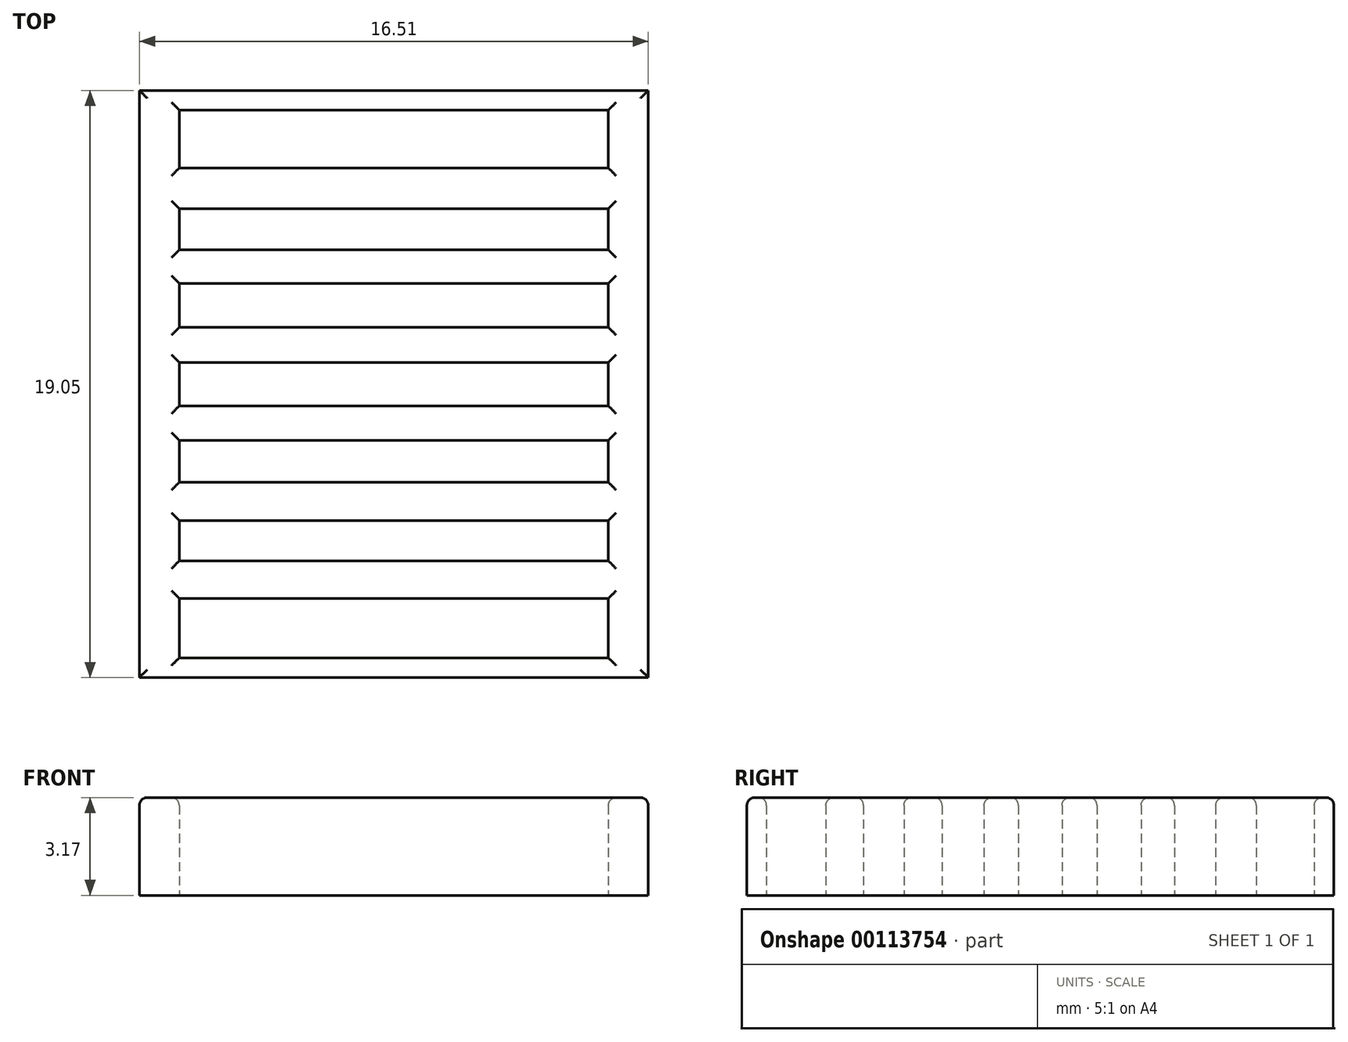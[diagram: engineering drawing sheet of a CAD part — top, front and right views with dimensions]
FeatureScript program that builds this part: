
annotation { "Feature Type Name" : "Feature", "Feature Type Description" : "" }
export const myFeature = defineFeature(function(context is Context, id is Id, definition is map)
    precondition{}
    {
        {
            var Q0;
            Q0=qCreatedBy(makeId("Top.planeOp"),FACE);
            var sketch = newSketch(context, id + "F0", { "sketchPlane" : qUnion([Q0])});
            skLineSegment(sketch, "E0.bottom", {"start": v(7.13, 8.73) * mm, "end": v(-6.8, 8.73) * mm});
            skLineSegment(sketch, "E0.top", {"start": v(7.13, -9.05) * mm, "end": v(-6.8, -9.05) * mm});
            skLineSegment(sketch, "E0.left", {"start": v(7.13, 8.73) * mm, "end": v(7.13, 6.84) * mm});
            skLineSegment(sketch, "E0.right", {"start": v(-6.8, 8.73) * mm, "end": v(-6.8, 6.84) * mm});
            skPoint(sketch, "E0.middle", {"position": v(0.16, -0.16) * mm});
            skPoint(sketch, "E1.orphan", {"position": v(-6.8, -0.16) * mm});
            skPoint(sketch, "E2.start.orphan", {"position": v(7.13, -0.16) * mm});
            skLineSegment(sketch, "E3.bottom", {"start": v(8.42, 9.36) * mm, "end": v(-8.1, 9.36) * mm});
            skLineSegment(sketch, "E3.top", {"start": v(8.42, -9.69) * mm, "end": v(-8.1, -9.69) * mm});
            skLineSegment(sketch, "E3.left", {"start": v(8.42, 9.36) * mm, "end": v(8.42, -9.69) * mm});
            skLineSegment(sketch, "E3.right", {"start": v(-8.1, 9.36) * mm, "end": v(-8.1, -9.69) * mm});
            skLineSegment(sketch, "E4.bottom", {"start": v(7.13, 5.53) * mm, "end": v(-6.8, 5.53) * mm});
            skLineSegment(sketch, "E4.top", {"start": v(7.13, 6.84) * mm, "end": v(-6.8, 6.84) * mm});
            skPoint(sketch, "E4.middle", {"position": v(0.16, 6.19) * mm});
            skLineSegment(sketch, "E5.bottom", {"start": v(7.13, 3.1) * mm, "end": v(-6.8, 3.1) * mm});
            skLineSegment(sketch, "E5.top", {"start": v(7.13, 4.19) * mm, "end": v(-6.8, 4.19) * mm});
            skPoint(sketch, "E5.middle", {"position": v(0.16, 3.65) * mm});
            skLineSegment(sketch, "E6.bottom", {"start": v(7.13, 0.54) * mm, "end": v(-6.8, 0.54) * mm});
            skLineSegment(sketch, "E6.top", {"start": v(7.13, 1.67) * mm, "end": v(-6.8, 1.67) * mm});
            skPoint(sketch, "E6.middle", {"position": v(0.16, 1.1) * mm});
            skLineSegment(sketch, "E7.bottom", {"start": v(7.13, -2) * mm, "end": v(-6.8, -2) * mm});
            skLineSegment(sketch, "E7.top", {"start": v(7.13, -0.88) * mm, "end": v(-6.8, -0.88) * mm});
            skPoint(sketch, "E7.middle", {"position": v(0.16, -1.43) * mm});
            skLineSegment(sketch, "E8.bottom", {"start": v(7.13, -4.6) * mm, "end": v(-6.8, -4.6) * mm});
            skLineSegment(sketch, "E8.top", {"start": v(7.13, -3.36) * mm, "end": v(-6.8, -3.36) * mm});
            skPoint(sketch, "E8.middle", {"position": v(0.16, -3.97) * mm});
            skLineSegment(sketch, "E9.bottom", {"start": v(7.13, -7.12) * mm, "end": v(-6.8, -7.12) * mm});
            skLineSegment(sketch, "E9.top", {"start": v(7.13, -5.9) * mm, "end": v(-6.8, -5.9) * mm});
            skPoint(sketch, "E9.middle", {"position": v(0.16, -6.51) * mm});
            skLineSegment(sketch, "E10.trimOffspring", {"start": v(-6.8, 5.53) * mm, "end": v(-6.8, 4.19) * mm});
            skLineSegment(sketch, "E11.trimOffspring", {"start": v(-6.8, 3.1) * mm, "end": v(-6.8, 1.67) * mm});
            skLineSegment(sketch, "E12.trimOffspring", {"start": v(-6.8, 0.54) * mm, "end": v(-6.8, -0.16) * mm});
            skLineSegment(sketch, "E13.trimOffspring", {"start": v(-6.8, -2) * mm, "end": v(-6.8, -3.36) * mm});
            skLineSegment(sketch, "E14.trimOffspring", {"start": v(-6.8, -4.6) * mm, "end": v(-6.8, -5.9) * mm});
            skLineSegment(sketch, "E15.trimOffspring", {"start": v(-6.8, -7.12) * mm, "end": v(-6.8, -9.05) * mm});
            skLineSegment(sketch, "E16.trimOffspring", {"start": v(7.13, -7.12) * mm, "end": v(7.13, -9.05) * mm});
            skLineSegment(sketch, "E17.trimOffspring", {"start": v(7.13, -4.6) * mm, "end": v(7.13, -5.9) * mm});
            skLineSegment(sketch, "E18.trimOffspring", {"start": v(7.13, -2) * mm, "end": v(7.13, -3.36) * mm});
            skLineSegment(sketch, "E19.trimOffspring", {"start": v(7.13, 0.54) * mm, "end": v(7.13, -0.88) * mm});
            skLineSegment(sketch, "E20.trimOffspring", {"start": v(7.13, 3.1) * mm, "end": v(7.13, 1.67) * mm});
            skLineSegment(sketch, "E21.trimOffspring", {"start": v(7.13, 5.53) * mm, "end": v(7.13, 4.19) * mm});
            skLineSegment(sketch, "E22", {"start": v(-6.8, -0.88) * mm, "end": v(-6.8, -0.16) * mm});
            skSolve(sketch);
        }
        {
            var Q0;
            Q0=makeQuery(id+"F0.imprint","IMPRINT",FACE,{"disambiguationData":[TD([[makeQuery(id+"F0.imprint","IMPRINT",EDGE,{"derivedFrom":sQuery(id+"F0.wireOp",EDGE,"E0.bottom")}),-1.0]])]});
            extrude(context, id + "F1", {"entities" : qUnion([Q0]), "depth" : 3.17 * mm});
        }
        {
            var Q0;
            Q0=makeQuery(id+"F1.opExtrude","CAP_FACE",FACE,{"disambiguationData":[OSD([sQuery(id+"F0.wireOp",EDGE,"E0.bottom"),sQuery(id+"F0.wireOp",EDGE,"E0.top"),sQuery(id+"F0.wireOp",EDGE,"E0.left"),sQuery(id+"F0.wireOp",EDGE,"E0.right"),sQuery(id+"F0.wireOp",EDGE,"E3.bottom"),sQuery(id+"F0.wireOp",EDGE,"E3.top"),sQuery(id+"F0.wireOp",EDGE,"E3.left"),sQuery(id+"F0.wireOp",EDGE,"E3.right"),sQuery(id+"F0.wireOp",EDGE,"E4.bottom"),sQuery(id+"F0.wireOp",EDGE,"E4.top"),sQuery(id+"F0.wireOp",EDGE,"E5.bottom"),sQuery(id+"F0.wireOp",EDGE,"E5.top"),sQuery(id+"F0.wireOp",EDGE,"E6.bottom"),sQuery(id+"F0.wireOp",EDGE,"E6.top"),sQuery(id+"F0.wireOp",EDGE,"E7.bottom"),sQuery(id+"F0.wireOp",EDGE,"E7.top"),sQuery(id+"F0.wireOp",EDGE,"E8.bottom"),sQuery(id+"F0.wireOp",EDGE,"E8.top"),sQuery(id+"F0.wireOp",EDGE,"E9.bottom"),sQuery(id+"F0.wireOp",EDGE,"E9.top"),sQuery(id+"F0.wireOp",EDGE,"E10.trimOffspring"),sQuery(id+"F0.wireOp",EDGE,"E11.trimOffspring"),sQuery(id+"F0.wireOp",EDGE,"E12.trimOffspring"),sQuery(id+"F0.wireOp",EDGE,"E13.trimOffspring"),sQuery(id+"F0.wireOp",EDGE,"E14.trimOffspring"),sQuery(id+"F0.wireOp",EDGE,"E15.trimOffspring"),sQuery(id+"F0.wireOp",EDGE,"E16.trimOffspring"),sQuery(id+"F0.wireOp",EDGE,"E17.trimOffspring"),sQuery(id+"F0.wireOp",EDGE,"E18.trimOffspring"),sQuery(id+"F0.wireOp",EDGE,"E19.trimOffspring"),sQuery(id+"F0.wireOp",EDGE,"E20.trimOffspring"),sQuery(id+"F0.wireOp",EDGE,"E21.trimOffspring"),sQuery(id+"F0.wireOp",EDGE,"E22")])],"isStart":false});
            fillet(context, id + "F2", {"entities" : qUnion([Q0]), "radius" : 0.25 * mm, "tangentPropagation" : true, "allowEdgeOverflow" : false});
        }
    });
